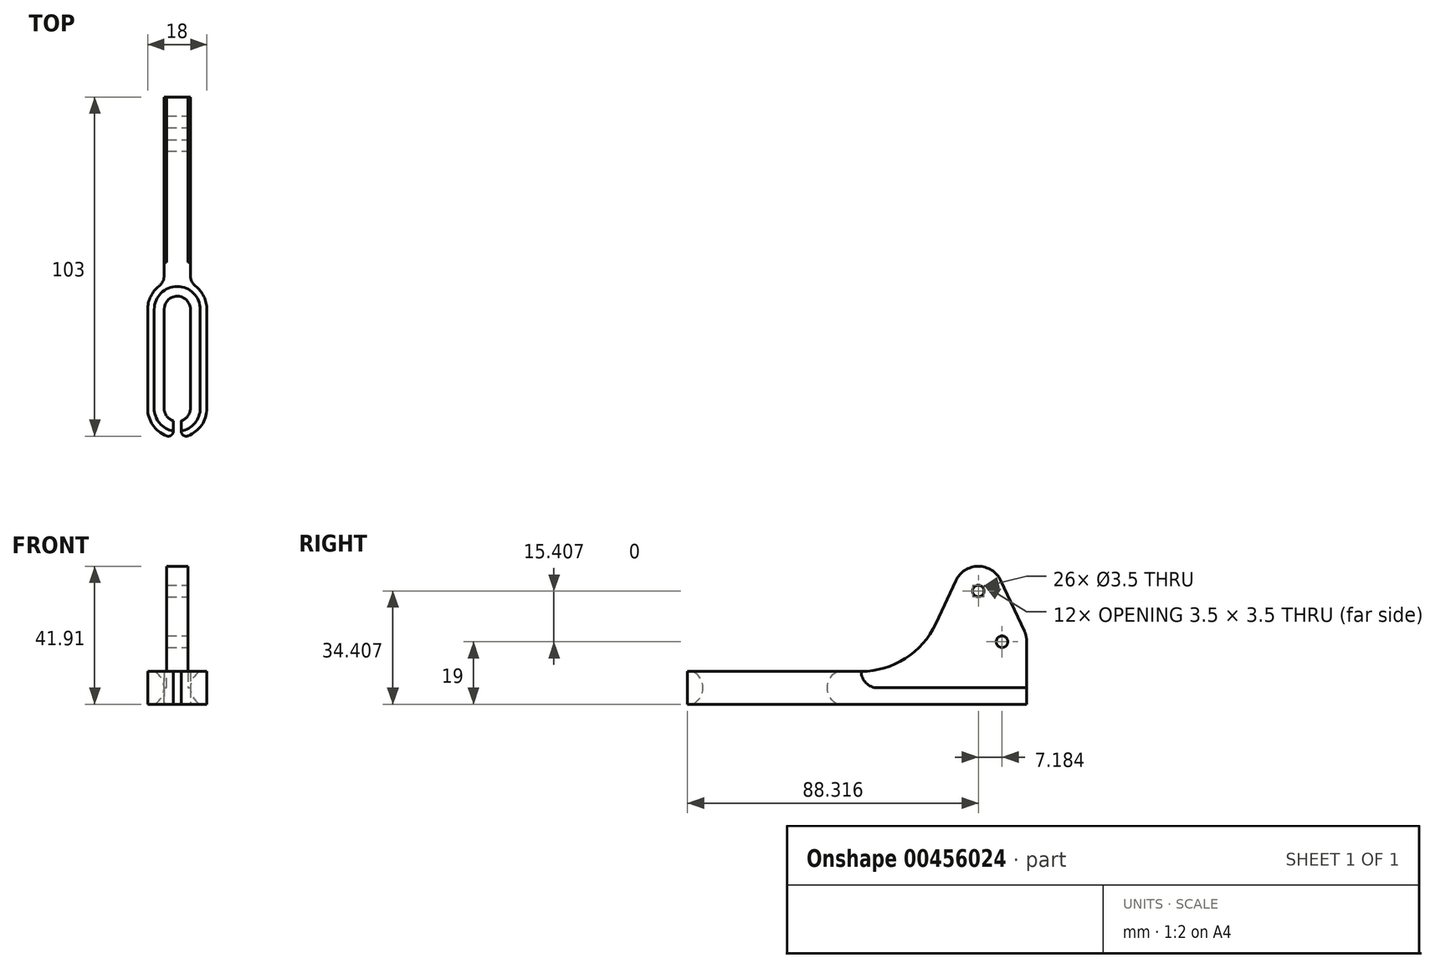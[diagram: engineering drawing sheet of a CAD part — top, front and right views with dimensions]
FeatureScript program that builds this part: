
annotation { "Feature Type Name" : "Feature", "Feature Type Description" : "" }
export const myFeature = defineFeature(function(context is Context, id is Id, definition is map)
    precondition{}
    {
        {
            var Q0;
            Q0=qCreatedBy(makeId("Top.planeOp"),FACE);
            var sketch = newSketch(context, id + "F0", { "sketchPlane" : qUnion([Q0])});
            skCircle(sketch, "E0", {"center": v(0, 0) * mm, "radius": 15 * mm, "construction": true});
            skLineSegment(sketch, "E1", {"start": v(-49.44, 35) * mm, "end": v(52.04, 35) * mm, "construction": true});
            skLineSegment(sketch, "E2.0", {"start": v(-49.44, 15) * mm, "end": v(52.04, 15) * mm, "construction": true});
            skLineSegment(sketch, "E3.0", {"start": v(-49.44, -15) * mm, "end": v(52.04, -15) * mm, "construction": true});
            skArc(sketch, "E4", {"start": v(-9, -15) * mm, "mid": v(0, -24) * mm, "end": v(9, -15) * mm});
            skArc(sketch, "E5", {"start": v(9, 15) * mm, "mid": v(8.09, 18.95) * mm, "end": v(5.54, 22.1) * mm});
            skLineSegment(sketch, "E6", {"start": v(-9, 15) * mm, "end": v(-9, -15) * mm});
            skLineSegment(sketch, "E7", {"start": v(9, 15) * mm, "end": v(9, -15) * mm});
            skLineSegment(sketch, "E8", {"start": v(-4, 25.25) * mm, "end": v(-4, 85) * mm});
            skLineSegment(sketch, "E9", {"start": v(-4, 85) * mm, "end": v(4, 85) * mm});
            skLineSegment(sketch, "E10", {"start": v(4, 85) * mm, "end": v(4, 25.25) * mm});
            skArc(sketch, "E11.trimOffspring", {"start": v(-5.54, 22.1) * mm, "mid": v(-8.09, 18.95) * mm, "end": v(-9, 15) * mm});
            skPoint(sketch, "E12.visualSharp", {"position": v(-4, 23.06) * mm});
            skArc(sketch, "E12.filletArc", {"start": v(-5.54, 22.1) * mm, "mid": v(-4.4, 23.5) * mm, "end": v(-4, 25.25) * mm});
            skPoint(sketch, "E13.visualSharp", {"position": v(4, 23.06) * mm});
            skArc(sketch, "E13.filletArc", {"start": v(4, 25.25) * mm, "mid": v(4.4, 23.5) * mm, "end": v(5.54, 22.1) * mm});
            skSolve(sketch);
        }
        {
            var Q0;
            Q0 = qSketchRegion(id + "F0", true);
            extrude(context, id + "F1", {"entities" : qUnion([Q0]), "depth" : 45 * mm});
        }
        {
            var Q0;
            Q0=qCreatedBy(makeId("Right.planeOp"),FACE);
            var sketch = newSketch(context, id + "F2", { "sketchPlane" : qUnion([Q0])});
            skLineSegment(sketch, "E14", {"start": v(-27.9, 10) * mm, "end": v(29.23, 10) * mm});
            skArc(sketch, "E15", {"start": v(71.61, 37.58) * mm, "mid": v(64.82, 41.9) * mm, "end": v(58.02, 37.58) * mm});
            skPoint(sketch, "E16", {"position": v(72, 19) * mm});
            skLineSegment(sketch, "E17", {"start": v(72, 19) * mm, "end": v(64.82, 34.4) * mm, "construction": true});
            skLineSegment(sketch, "E18.0", {"start": v(78.8, 22.17) * mm, "end": v(71.61, 37.58) * mm});
            skLineSegment(sketch, "E19", {"start": v(79.5, 19) * mm, "end": v(79.5, 0) * mm});
            skLineSegment(sketch, "E20", {"start": v(58.02, 37.58) * mm, "end": v(51.89, 24.43) * mm});
            skLineSegment(sketch, "E21", {"start": v(64.82, 34.4) * mm, "end": v(64.82, -17.98) * mm, "construction": true});
            skPoint(sketch, "E22.visualSharp", {"position": v(45.16, 10) * mm});
            skArc(sketch, "E22.filletArc", {"start": v(29.23, 10) * mm, "mid": v(42.66, 13.92) * mm, "end": v(51.89, 24.43) * mm});
            skLineSegment(sketch, "E23", {"start": v(-27.9, 10) * mm, "end": v(-27.9, 46.34) * mm});
            skLineSegment(sketch, "E24", {"start": v(-27.9, 46.34) * mm, "end": v(96.84, 46.34) * mm});
            skLineSegment(sketch, "E25", {"start": v(96.84, 46.34) * mm, "end": v(96.84, 0) * mm});
            skLineSegment(sketch, "E26", {"start": v(96.84, 0) * mm, "end": v(79.5, 0) * mm});
            skArc(sketch, "E27.trimOffspring", {"start": v(79.5, 19) * mm, "mid": v(79.32, 20.62) * mm, "end": v(78.8, 22.17) * mm});
            skSolve(sketch);
        }
        {
            var Q0;
            Q0 = qSketchRegion(id + "F2", true);
            extrude(context, id + "F3", {"entities" : qUnion([Q0]), "operationType" : NewBodyOperationType.REMOVE, "endBound" : BoundingType.THROUGH_ALL, "oppositeDirection" : true, "depth" : 15 * mm, "hasSecondDirection" : true, "secondDirectionBound" : SecondDirectionBoundingType.THROUGH_ALL, "secondDirectionOppositeDirection" : false, "secondDirectionDepth" : 25 * mm});
        }
        {
            var Q0;
            Q0=makeQuery(id+"F3.boolean.opBoolean","COPY",FACE,{"derivedFrom":makeQuery(id+"F3.opExtrude","SWEPT_FACE",FACE,{"disambiguationData":[OSD([sQuery(id+"F2.wireOp",EDGE,"E19")])]})});
            var sketch = newSketch(context, id + "F4", { "sketchPlane" : qUnion([Q0])});
            skLineSegment(sketch, "E28", {"start": v(-3.2, 5) * mm, "end": v(-5, 5) * mm});
            skLineSegment(sketch, "E29", {"start": v(-5, 5) * mm, "end": v(-5, 44.9) * mm});
            skLineSegment(sketch, "E30", {"start": v(-5, 44.9) * mm, "end": v(5, 44.9) * mm});
            skLineSegment(sketch, "E31", {"start": v(5, 44.9) * mm, "end": v(5, 5) * mm});
            skLineSegment(sketch, "E32", {"start": v(5, 5) * mm, "end": v(3.2, 5) * mm});
            skLineSegment(sketch, "E33", {"start": v(3.2, 5) * mm, "end": v(3.2, 42.9) * mm});
            skLineSegment(sketch, "E34", {"start": v(3.2, 42.9) * mm, "end": v(-3.2, 42.9) * mm});
            skLineSegment(sketch, "E35", {"start": v(-3.2, 42.9) * mm, "end": v(-3.2, 5) * mm});
            skSolve(sketch);
        }
        {
            var Q0;
            Q0 = qSketchRegion(id + "F4", true);
            extrude(context, id + "F5", {"entities" : qUnion([Q0]), "operationType" : NewBodyOperationType.REMOVE, "oppositeDirection" : true, "depth" : 50.25 * mm});
        }
        {
            var Q0;
            Q0=makeQuery(id+"F5.boolean.opBoolean","COPY",EDGE,{"derivedFrom":makeQuery(id+"F5.opExtrude","CAP_EDGE",EDGE,{"disambiguationData":[OSD([sQuery(id+"F4.wireOp",EDGE,"E28")])],"isStart":false})});
            var Q1;
            Q1=makeQuery(id+"F5.boolean.opBoolean","COPY",EDGE,{"derivedFrom":makeQuery(id+"F5.opExtrude","CAP_EDGE",EDGE,{"disambiguationData":[OSD([sQuery(id+"F4.wireOp",EDGE,"E32")])],"isStart":false})});
            fillet(context, id + "F6", {"entities" : qUnion([Q0, Q1]), "radius" : 5 * mm, "tangentPropagation" : true, "allowEdgeOverflow" : false});
        }
        {
            var Q0;
            Q0=makeQuery(id+"F5.boolean.opBoolean","COPY",FACE,{"derivedFrom":makeQuery(id+"F5.opExtrude","SWEPT_FACE",FACE,{"disambiguationData":[OSD([sQuery(id+"F4.wireOp",EDGE,"E35")])]})});
            var sketch = newSketch(context, id + "F7", { "sketchPlane" : qUnion([Q0])});
            skPoint(sketch, "E36.0", {"position": v(72, 19) * mm});
            skPoint(sketch, "E37.0", {"position": v(64.82, 34.4) * mm});
            skSolve(sketch);
        }
        {
            var Q0;
            Q0=sQuery(id+"F7.wireOp",VERTEX,"E37.0");
            var Q1;
            Q1=sQuery(id+"F7.wireOp",VERTEX,"E36.0");
            var Q2;
            Q2=makeQuery(id+"F1.opExtrude","SWEPT_BODY",BODY,{"disambiguationData":[OSD([sQuery(id+"F0.wireOp",EDGE,"E4"),sQuery(id+"F0.wireOp",EDGE,"E5"),sQuery(id+"F0.wireOp",EDGE,"E6"),sQuery(id+"F0.wireOp",EDGE,"E7"),sQuery(id+"F0.wireOp",EDGE,"E8"),sQuery(id+"F0.wireOp",EDGE,"E9"),sQuery(id+"F0.wireOp",EDGE,"E10"),sQuery(id+"F0.wireOp",EDGE,"E11.trimOffspring"),sQuery(id+"F0.wireOp",EDGE,"E12.filletArc"),sQuery(id+"F0.wireOp",EDGE,"E13.filletArc")])]});
            hole(context, id + "F8", {"style" : HoleStyle.SIMPLE, "endStyle" : HoleEndStyle.THROUGH, "holeDiameter" : 3.5 * mm, "isTappedThrough" : true, "tappedDepth" : 12 * mm, "tapClearance" : 3, "startFromSketch" : true, "locations" : qUnion([Q0, Q1]), "scope" : qUnion([Q2])});
        }
        {
            var Q0;
            Q0=makeQuery(id+"F1.opExtrude","CAP_FACE",FACE,{"disambiguationData":[OSD([sQuery(id+"F0.wireOp",EDGE,"E4"),sQuery(id+"F0.wireOp",EDGE,"E5"),sQuery(id+"F0.wireOp",EDGE,"E6"),sQuery(id+"F0.wireOp",EDGE,"E7"),sQuery(id+"F0.wireOp",EDGE,"E8"),sQuery(id+"F0.wireOp",EDGE,"E9"),sQuery(id+"F0.wireOp",EDGE,"E10"),sQuery(id+"F0.wireOp",EDGE,"E11.trimOffspring"),sQuery(id+"F0.wireOp",EDGE,"E12.filletArc"),sQuery(id+"F0.wireOp",EDGE,"E13.filletArc")])],"isStart":true});
            var sketch = newSketch(context, id + "F9", { "sketchPlane" : qUnion([Q0])});
            skLineSegment(sketch, "E38", {"start": v(0, 15) * mm, "end": v(0, -15) * mm, "construction": true});
            skArc(sketch, "E39.0.startCap", {"start": v(-7, 15) * mm, "mid": v(0, 22) * mm, "end": v(7, 15) * mm});
            skArc(sketch, "E39.0.endCap", {"start": v(7, -15) * mm, "mid": v(0, -22) * mm, "end": v(-7, -15) * mm});
            skLineSegment(sketch, "E39.0.left", {"start": v(7, 15) * mm, "end": v(7, -15) * mm});
            skLineSegment(sketch, "E39.0.right", {"start": v(-7, 15) * mm, "end": v(-7, -15) * mm});
            skSolve(sketch);
        }
        {
            var Q0;
            Q0=qCreatedBy(makeId("Front.planeOp"),FACE);
            var sketch = newSketch(context, id + "F10", { "sketchPlane" : qUnion([Q0])});
            skPoint(sketch, "E40.0", {"position": v(7, 0) * mm});
            skArc(sketch, "E41", {"start": v(7, 10) * mm, "mid": v(4, 5) * mm, "end": v(7, 0) * mm});
            skLineSegment(sketch, "E42", {"start": v(7, 0) * mm, "end": v(0, 0) * mm});
            skLineSegment(sketch, "E43", {"start": v(0, 0) * mm, "end": v(0, 10) * mm, "construction": true});
            skLineSegment(sketch, "E44", {"start": v(0, 10) * mm, "end": v(7, 10) * mm});
            skLineSegment(sketch, "E45.MirrorCS", {"start": v(-7, 0) * mm, "end": v(0, 0) * mm});
            skPoint(sketch, "E46.MirrorP", {"position": v(-7, 0) * mm});
            skArc(sketch, "E47.MirrorCS", {"start": v(-7, 10) * mm, "mid": v(-4, 5) * mm, "end": v(-7, 0) * mm});
            skLineSegment(sketch, "E48.MirrorCS", {"start": v(0, 10) * mm, "end": v(-7, 10) * mm});
            skSolve(sketch);
        }
        {
            var Q0;
            Q0 = qSketchRegion(id + "F10", true);
            extrude(context, id + "F11", {"entities" : qUnion([Q0]), "operationType" : NewBodyOperationType.REMOVE, "oppositeDirection" : true, "depth" : 15 * mm, "hasSecondDirection" : true, "secondDirectionOppositeDirection" : false, "secondDirectionDepth" : 15 * mm});
        }
        {
            var Q0;
            Q0=makeQuery(id+"F11.boolean.opBoolean","COPY",FACE,{"derivedFrom":makeQuery(id+"F11.opExtrude","CAP_FACE",FACE,{"disambiguationData":[OSD([sQuery(id+"F10.wireOp",EDGE,"E41"),sQuery(id+"F10.wireOp",EDGE,"E42"),sQuery(id+"F10.wireOp",EDGE,"E44"),sQuery(id+"F10.wireOp",EDGE,"E45.MirrorCS"),sQuery(id+"F10.wireOp",EDGE,"E47.MirrorCS"),sQuery(id+"F10.wireOp",EDGE,"E48.MirrorCS")])],"isStart":true})});
            var sketch = newSketch(context, id + "F12", { "sketchPlane" : qUnion([Q0])});
            skLineSegment(sketch, "E49", {"start": v(0, 10) * mm, "end": v(0, -9.65) * mm, "construction": true});
            skArc(sketch, "E50.0", {"start": v(7, 10) * mm, "mid": v(4, 5) * mm, "end": v(7, 0) * mm});
            skLineSegment(sketch, "E51.0", {"start": v(7, 0) * mm, "end": v(0, 0) * mm});
            skLineSegment(sketch, "E52.0", {"start": v(7, 10) * mm, "end": v(0, 10) * mm});
            skLineSegment(sketch, "E53", {"start": v(0, 10) * mm, "end": v(0, 0) * mm});
            skPoint(sketch, "E54.orphan", {"position": v(-7, 10) * mm});
            skPoint(sketch, "E55.orphan", {"position": v(-7, 0) * mm});
            skSolve(sketch);
        }
        {
            var Q0;
            Q0 = qSketchRegion(id + "F12", true);
            var Q1;
            Q1=sQuery(id+"F12.wireOp",EDGE,"E49");
            revolve(context, id + "F13", {"operationType" : NewBodyOperationType.REMOVE, "entities" : qUnion([Q0]), "axis" : qUnion([Q1]), "revolveType" : RevolveType.ONE_DIRECTION, "oppositeDirection" : true, "angle" : 180 * degree});
        }
        {
            var Q0;
            Q0=makeQuery(id+"F11.boolean.opBoolean","COPY",FACE,{"derivedFrom":makeQuery(id+"F11.opExtrude","CAP_FACE",FACE,{"disambiguationData":[OSD([sQuery(id+"F10.wireOp",EDGE,"E41"),sQuery(id+"F10.wireOp",EDGE,"E42"),sQuery(id+"F10.wireOp",EDGE,"E44"),sQuery(id+"F10.wireOp",EDGE,"E45.MirrorCS"),sQuery(id+"F10.wireOp",EDGE,"E47.MirrorCS"),sQuery(id+"F10.wireOp",EDGE,"E48.MirrorCS")])],"isStart":false})});
            var sketch = newSketch(context, id + "F14", { "sketchPlane" : qUnion([Q0])});
            skLineSegment(sketch, "E56", {"start": v(0, 10) * mm, "end": v(0, -7.3) * mm, "construction": true});
            skPoint(sketch, "E56.endSnap0", {"position": v(0, 10) * mm});
            skArc(sketch, "E57.0", {"start": v(-7, 10) * mm, "mid": v(-4, 5) * mm, "end": v(-7, 0) * mm});
            skLineSegment(sketch, "E58.0", {"start": v(-7, 10) * mm, "end": v(0, 10) * mm});
            skLineSegment(sketch, "E59.0", {"start": v(-7, 0) * mm, "end": v(0, 0) * mm});
            skPoint(sketch, "E60.orphan", {"position": v(7, 10) * mm});
            skPoint(sketch, "E61.orphan", {"position": v(7, 0) * mm});
            skLineSegment(sketch, "E62", {"start": v(0, 10) * mm, "end": v(0, 0) * mm});
            skSolve(sketch);
        }
        {
            var Q0;
            Q0 = qSketchRegion(id + "F14", true);
            var Q1;
            Q1=sQuery(id+"F14.wireOp",EDGE,"E56");
            revolve(context, id + "F15", {"operationType" : NewBodyOperationType.REMOVE, "entities" : qUnion([Q0]), "axis" : qUnion([Q1]), "revolveType" : RevolveType.ONE_DIRECTION, "angle" : 180 * degree});
        }
        {
            var Q0;
            Q0=qCreatedBy(makeId("Top.planeOp"),FACE);
            var sketch = newSketch(context, id + "F16", { "sketchPlane" : qUnion([Q0])});
            skLineSegment(sketch, "E63", {"start": v(0, -17.17) * mm, "end": v(0, -27.94) * mm, "construction": true});
            skLineSegment(sketch, "E64.0", {"start": v(-1.2, -17.17) * mm, "end": v(-1.2, -27.94) * mm});
            skLineSegment(sketch, "E65", {"start": v(-1.2, -27.94) * mm, "end": v(0, -27.94) * mm});
            skLineSegment(sketch, "E66", {"start": v(-1.2, -17.17) * mm, "end": v(0, -17.17) * mm});
            skLineSegment(sketch, "E67.MirrorCS", {"start": v(1.2, -17.17) * mm, "end": v(1.2, -27.94) * mm});
            skLineSegment(sketch, "E68.MirrorCS", {"start": v(1.2, -17.17) * mm, "end": v(0, -17.17) * mm});
            skLineSegment(sketch, "E69.MirrorCS", {"start": v(1.2, -27.94) * mm, "end": v(0, -27.94) * mm});
            skSolve(sketch);
        }
        {
            var Q0;
            Q0 = qSketchRegion(id + "F16", true);
            var Q1;
            Q1=makeQuery(id+"F3.boolean.opBoolean","COPY",FACE,{"derivedFrom":makeQuery(id+"F3.opExtrude","SWEPT_FACE",FACE,{"disambiguationData":[OSD([sQuery(id+"F2.wireOp",EDGE,"E14")])]})});
            extrude(context, id + "F17", {"entities" : qUnion([Q0]), "operationType" : NewBodyOperationType.REMOVE, "endBound" : BoundingType.UP_TO_SURFACE, "endBoundEntityFace" : qUnion([Q1]), "depth" : 25 * mm});
        }
        {
            var Q0;
            Q0=makeQuery(id+"F17.boolean.opBoolean","INTERSECT",EDGE,{"derivedFrom":[makeQuery(id+"F1.opExtrude","SWEPT_FACE",FACE,{"disambiguationData":[OSD([sQuery(id+"F0.wireOp",EDGE,"E4")])]}),makeQuery(id+"F17.opExtrude","SWEPT_FACE",FACE,{"disambiguationData":[OSD([sQuery(id+"F16.wireOp",EDGE,"E64.0")])]})]});
            var Q1;
            Q1=makeQuery(id+"F17.boolean.opBoolean","INTERSECT",EDGE,{"derivedFrom":[makeQuery(id+"F1.opExtrude","SWEPT_FACE",FACE,{"disambiguationData":[OSD([sQuery(id+"F0.wireOp",EDGE,"E4")])]}),makeQuery(id+"F17.opExtrude","SWEPT_FACE",FACE,{"disambiguationData":[OSD([sQuery(id+"F16.wireOp",EDGE,"E67.MirrorCS")])]})]});
            fillet(context, id + "F18", {"entities" : qUnion([Q0, Q1]), "radius" : 1.5 * mm, "tangentPropagation" : true, "allowEdgeOverflow" : false});
        }
    });
